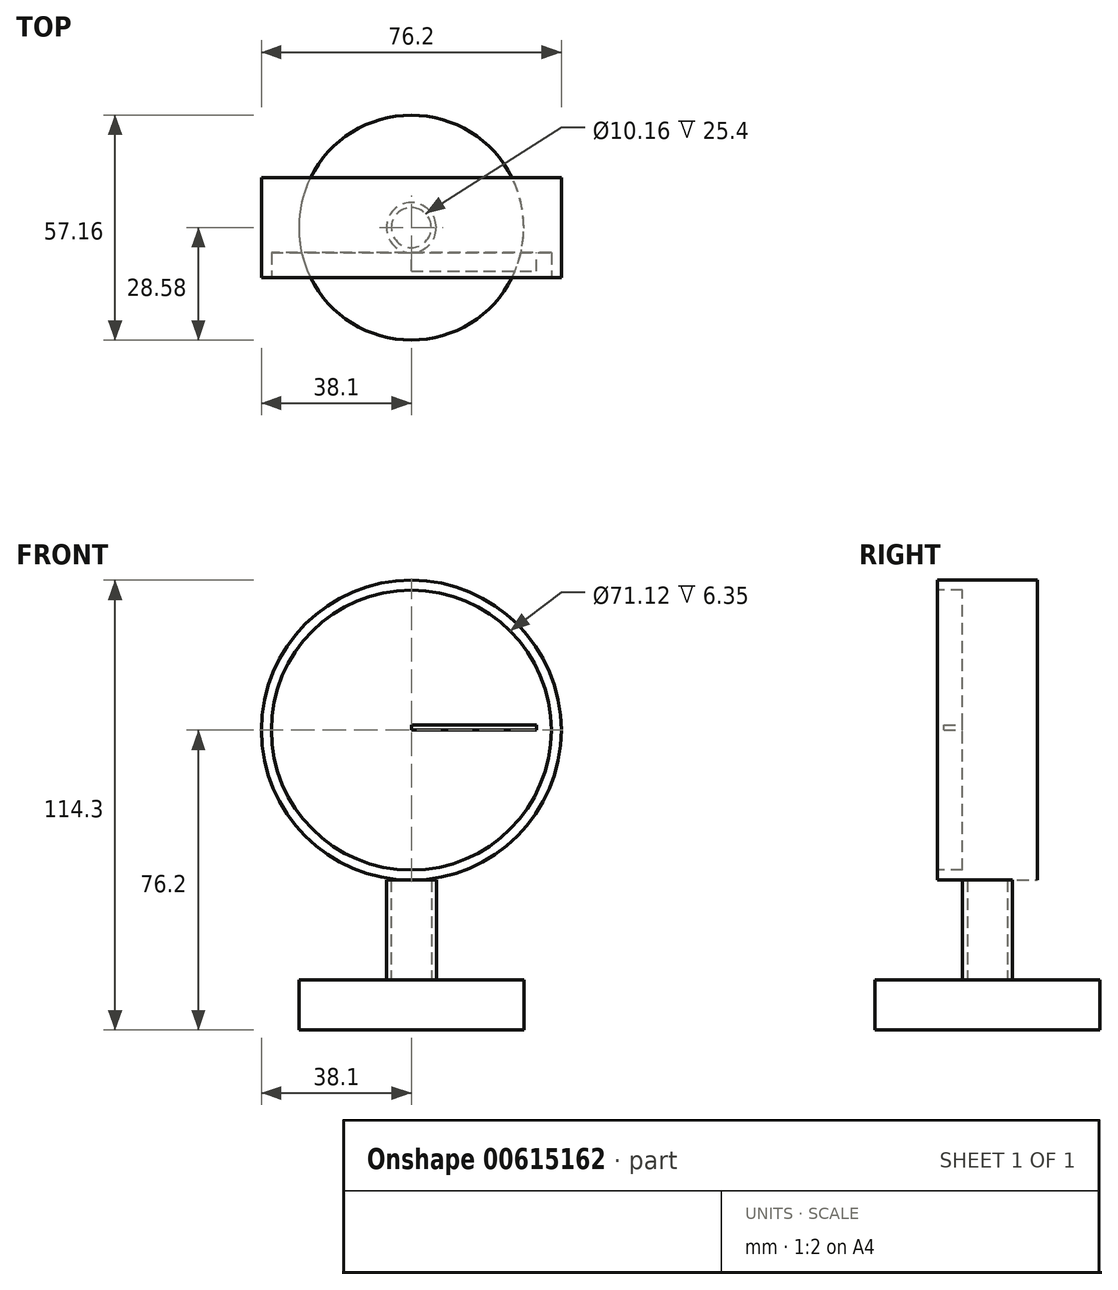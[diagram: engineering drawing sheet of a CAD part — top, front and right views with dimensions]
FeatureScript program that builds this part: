
annotation { "Feature Type Name" : "Feature", "Feature Type Description" : "" }
export const myFeature = defineFeature(function(context is Context, id is Id, definition is map)
    precondition{}
    {
        {
            var Q0;
            Q0=qCreatedBy(makeId("Top.planeOp"),FACE);
            var sketch = newSketch(context, id + "F0", { "sketchPlane" : qUnion([Q0])});
            skCircle(sketch, "E0", {"center": v(0, 0) * mm, "radius": 28.58 * mm});
            skSolve(sketch);
        }
        {
            var Q0;
            Q0 = qSketchRegion(id + "F0", true);
            extrude(context, id + "F1", {"entities" : qUnion([Q0]), "depth" : 12.7 * mm, "offsetDistance" : 25.4 * mm});
        }
        {
            var Q0;
            Q0=makeQuery(id+"F1.opExtrude","CAP_FACE",FACE,{"disambiguationData":[OSD([sQuery(id+"F0.wireOp",EDGE,"E0")])],"isStart":false});
            var sketch = newSketch(context, id + "F2", { "sketchPlane" : qUnion([Q0])});
            skCircle(sketch, "E1", {"center": v(0, 0) * mm, "radius": 6.35 * mm});
            skCircle(sketch, "E2", {"center": v(0, 0) * mm, "radius": 5.08 * mm});
            skSolve(sketch);
        }
        {
            var Q0;
            Q0 = qSketchRegion(id + "F2", true);
            extrude(context, id + "F3", {"entities" : qUnion([Q0]), "operationType" : NewBodyOperationType.ADD, "depth" : 25.4 * mm, "offsetDistance" : 25.4 * mm});
        }
        {
            var Q0;
            Q0=qCreatedBy(makeId("Front.planeOp"),FACE);
            var sketch = newSketch(context, id + "F4", { "sketchPlane" : qUnion([Q0])});
            skLineSegment(sketch, "E3", {"start": v(0, 0) * mm, "end": v(0, 38.1) * mm});
            skLineSegment(sketch, "E4", {"start": v(0, 38.1) * mm, "end": v(0, 76.2) * mm});
            skCircle(sketch, "E5", {"center": v(0, 76.2) * mm, "radius": 38.1 * mm});
            skSolve(sketch);
        }
        {
            var Q0;
            Q0 = qSketchRegion(id + "F4", true);
            extrude(context, id + "F5", {"entities" : qUnion([Q0]), "operationType" : NewBodyOperationType.ADD, "depth" : 25.4 * mm, "offsetDistance" : 25.4 * mm, "symmetric" : true});
        }
        {
            var Q0;
            Q0=makeQuery(id+"F5.opExtrude","CAP_FACE",FACE,{"disambiguationData":[OSD([sQuery(id+"F4.wireOp",EDGE,"E5")])],"isStart":false});
            var sketch = newSketch(context, id + "F6", { "sketchPlane" : qUnion([Q0])});
            skCircle(sketch, "E6", {"center": v(0, 76.2) * mm, "radius": 35.56 * mm});
            skSolve(sketch);
        }
        {
            var Q0;
            Q0 = qSketchRegion(id + "F6", true);
            extrude(context, id + "F7", {"entities" : qUnion([Q0]), "operationType" : NewBodyOperationType.REMOVE, "oppositeDirection" : true, "depth" : 6.35 * mm, "offsetDistance" : 25.4 * mm});
        }
        {
            var Q0;
            Q0=makeQuery(id+"F7.boolean.opBoolean","COPY",FACE,{"derivedFrom":makeQuery(id+"F7.opExtrude","CAP_FACE",FACE,{"disambiguationData":[OSD([sQuery(id+"F6.wireOp",EDGE,"E6")])],"isStart":false})});
            var sketch = newSketch(context, id + "F8", { "sketchPlane" : qUnion([Q0])});
            skLineSegment(sketch, "E7.bottom", {"start": v(0, 76.2) * mm, "end": v(31.75, 76.2) * mm});
            skLineSegment(sketch, "E7.top", {"start": v(0, 77.47) * mm, "end": v(31.75, 77.47) * mm});
            skLineSegment(sketch, "E7.left", {"start": v(0, 76.2) * mm, "end": v(0, 77.47) * mm});
            skLineSegment(sketch, "E7.right", {"start": v(31.75, 76.2) * mm, "end": v(31.75, 77.47) * mm});
            skSolve(sketch);
        }
        {
            var Q0;
            Q0 = qSketchRegion(id + "F8", true);
            extrude(context, id + "F9", {"entities" : qUnion([Q0]), "operationType" : NewBodyOperationType.ADD, "depth" : 4.75 * mm, "offsetDistance" : 25.4 * mm});
        }
    });
